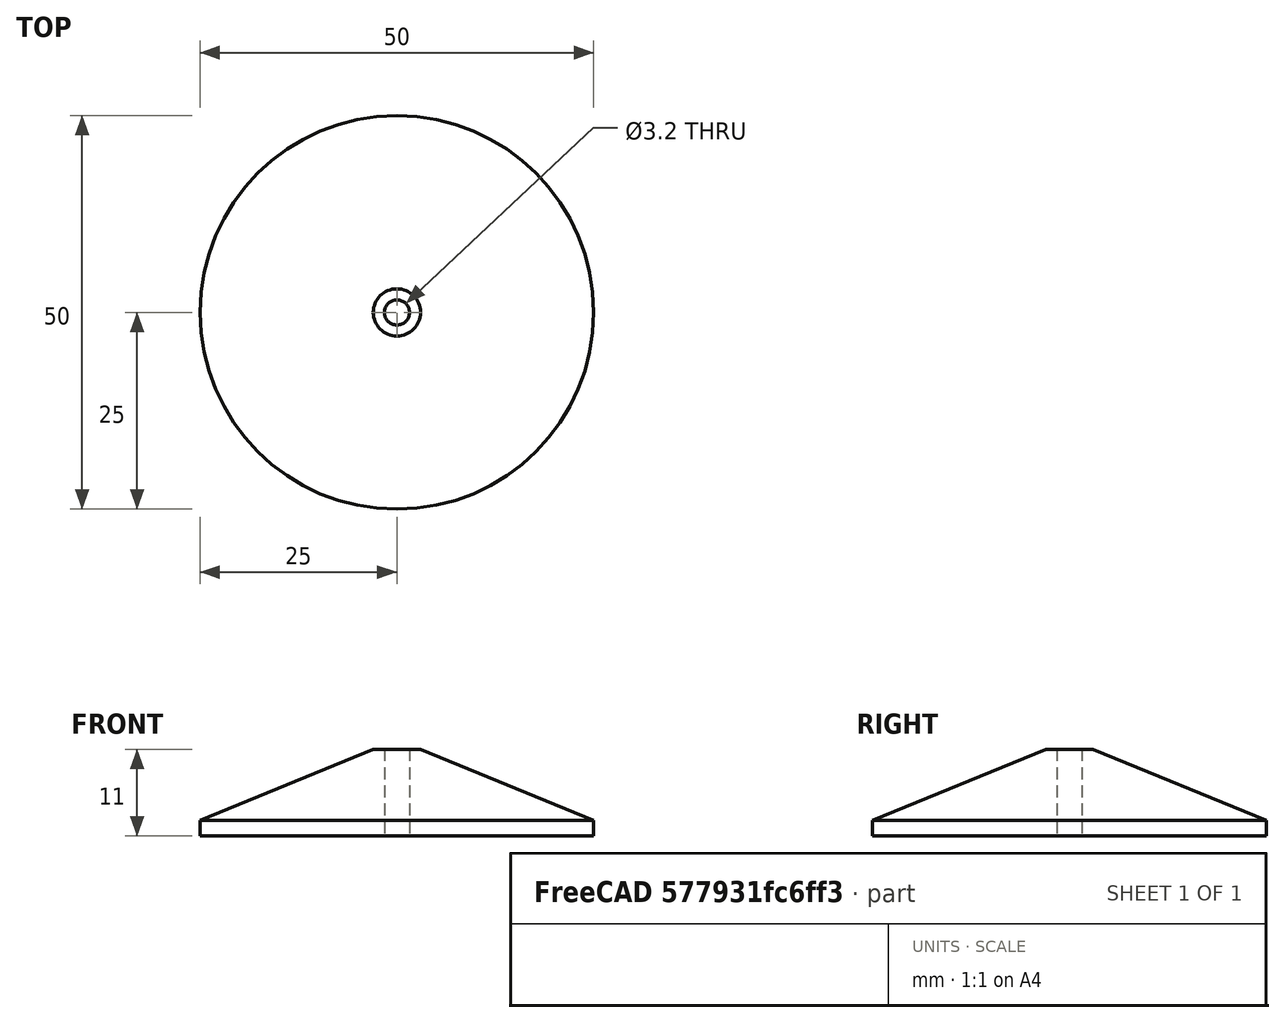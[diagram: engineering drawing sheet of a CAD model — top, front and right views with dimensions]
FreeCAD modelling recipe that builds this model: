
FCSTD DOCUMENT  (FreeCAD 0.21R33668 +26 (Git))
Label: BobbinSocket_Big_R_A2
License: All rights reserved
LicenseURL: http://en.wikipedia.org/wiki/All_rights_reserved
objects: Sketcher::SketchObject×1, PartDesign::Revolution×1, PartDesign::Body×1, App::Part×1
note: 4 computed .brp shape members not serialized (recipe doc carries the construction recipe); baked Part::Feature solids carry a one-line shape summary decoded from their .brp

FEATURE [Sketcher::SketchObject] Sketch002
  FullyConstrained = false
  MapMode = 5
  Placement = pos=(0,0,0) rot=(0.57735,0.57735,0.57735;2.0944rad)
  Support = -> [YZ_Plane001]
  sketch-geometry (5):
    g0: LineSegment StartX=1.6 StartY=11.0004 StartZ=0 EndX=1.6 EndY=0 EndZ=0
    g1: LineSegment StartX=25 StartY=0 StartZ=0 EndX=25 EndY=2 EndZ=0
    g2: LineSegment StartX=1.6 StartY=0 StartZ=0 EndX=25 EndY=0 EndZ=0
    g3: LineSegment StartX=1.6 StartY=11.0004 StartZ=0 EndX=3 EndY=11.0004 EndZ=0
    g4: LineSegment StartX=3 StartY=11.0004 StartZ=0 EndX=25 EndY=2 EndZ=0
  constraints (15):
    c: PointOnObject(g1,g-1)
    c: Vertical(g1)
    c: DistanceX(g-1,g0) = 1.6
    c: Vertical(g0)
    c: PointOnObject(g2,g-1)
    c: Coincident(g2,g1)
    c: DistanceX(g-1,g1) = 25
    c: Coincident(g0,g3)
    c: Horizontal(g3)
    c: Coincident(g3,g4)
    c: Coincident(g4,g1)
    c: DistanceX(g-1,g3) = 3
    c: Angle(g4,g2) = 0.388336
    c: Coincident(g2,g0)
    c: DistanceY(g1,g1) = 2
FEATURE [PartDesign::Revolution] Revolution
  AllowMultiFace = false
  Angle = 360
  Axis = (0,0,1)
  Base = (0,0,0)
  Placement = pos=(0,0,0) rot=(0.57735,0.57735,0.57735;2.0944rad)
  Profile = -> Sketch002
  ReferenceAxis = -> Sketch002 [V_Axis]
  Reversed = true
FEATURE [PartDesign::Body] RevolutionBody
  Group = -> [Sketch002,Revolution]
  Origin = -> Origin001
  Tip = -> Revolution
FEATURE [App::Part] Part
  Group = -> [RevolutionBody]
  License = CC BY 3.0
  LicenseURL = http://creativecommons.org/licenses/by/3.0/
  Origin = -> Origin
